# Revit family: ASSA_ABLOY_SecurityPortal_EL_Twin
name_source: partatom
category: Doors
units: mm (PartAtom-declared; Revit-internal decimal feet)

## family parameters
Always vertical = Yes
Cut with Voids When Loaded = No
Room Calculation Point = No
Shared = No
Work Plane-Based = No

## types (1)
- EL Twin
    Advance = Yes
    Alarm = agtatec_Record_Glass
    Analytic Construction = <None>
    AntiFingerTrapRequirement = No
    BIMObjectName = ASSA_ABLOY_SecurityPortals_EL_Twin
    CanopyHeight = 211.00 mm
    Capacity = up tp 2000 people / hour
    Color = RAL
    Construction Type = Automatic Sliding Door
    Cost = 0 $
    Define Thermal Properties by = Schematic Type
    DoorIncluded = Yes
    DoorSeal = Yes
    ElectronicLock = Yes
    Features = Throw-In detection
    Finish = Aluminium and Glass
    FrameFinishOptions = stainless steel finish
    FrameMaterial = agtatec_Record_Aluminium
    Frames = agtatec_Record_Aluminium
    Function = Exterior
    GlassLayers = 1
    GlassThickness1 = 8.20 mm
    HandicapAccessible = No
    HasDrive = Yes
    Height = 500.00 mm
    HeightLimit = 2150.00 mm
    Heightmax = 2300.00 mm
    Heightmin = 2150.00 mm
    IfcExportAs = IFCDoorStyle
    IfcExportType = Door
    IsExternal = No
    Length = 5999.84 mm
    ManufacturerURL = www.agta-record.com
    Material = Aluminium
    ModelReference = depends on the configuration
    NBSDescription = Sliding Doorset
    NBSReference = 25-50-20/176
    Name = record FlipFlow Twin
    NominalHeight = 500.00 mm
    NominalLength = 3526.00 mm
    NominalWidth = 979.00 mm
    OpenDoor = No
    OpeningRotationAngle = 0.00°
    Operation = Automatic
    PanelGlass = agtatec_Record_Glass
    PanelWidth = 573.10 mm
    PanelWidth2 = 623.10 mm
    PanelWidth3 = 348.10 mm
    Passage Width Input = 3
    PassageHeight = 2100.00 mm
    PassageWidth = 1100.00 mm
    PassageWidthF = 0.00 mm
    PassageWidthOptions = 650/900/1100/1203
    Rough Height = 500.00 mm
    Rough Width = 979.00 mm
    Row1 = No
    Row2 = Yes
    Row3 = Yes
    Rubber = agtatec_Record_Rubber
    SafetyDevices = YES
    Second Passage Width Input = 4
    SecondPassage = Yes
    SecondPassageWidth = 1200.00 mm
    SelfClosing = Yes
    Sensor = agtatec_Record_Aluminium
    Shape = cuboid shaped
    Size = 2365x3526x979
    SmokeStop = No
    Thickness = 0.00 mm
    Third Passage Width Input = 1
    ThirdPassage = Yes
    ThirdPassageWidth = 650.00 mm
    ThresholdRequired = No
    ThresholdStripping = No
    Uniclass2015Code = Pr_30_59_24_37
    Uniclass2015Title = High security doorsets
    Uniclass2015Version = 1.9
    Width = 979.00 mm

## geometry (parser evidence)
native form markers: Sweep x7
no freeform markers — native parametric forms only
